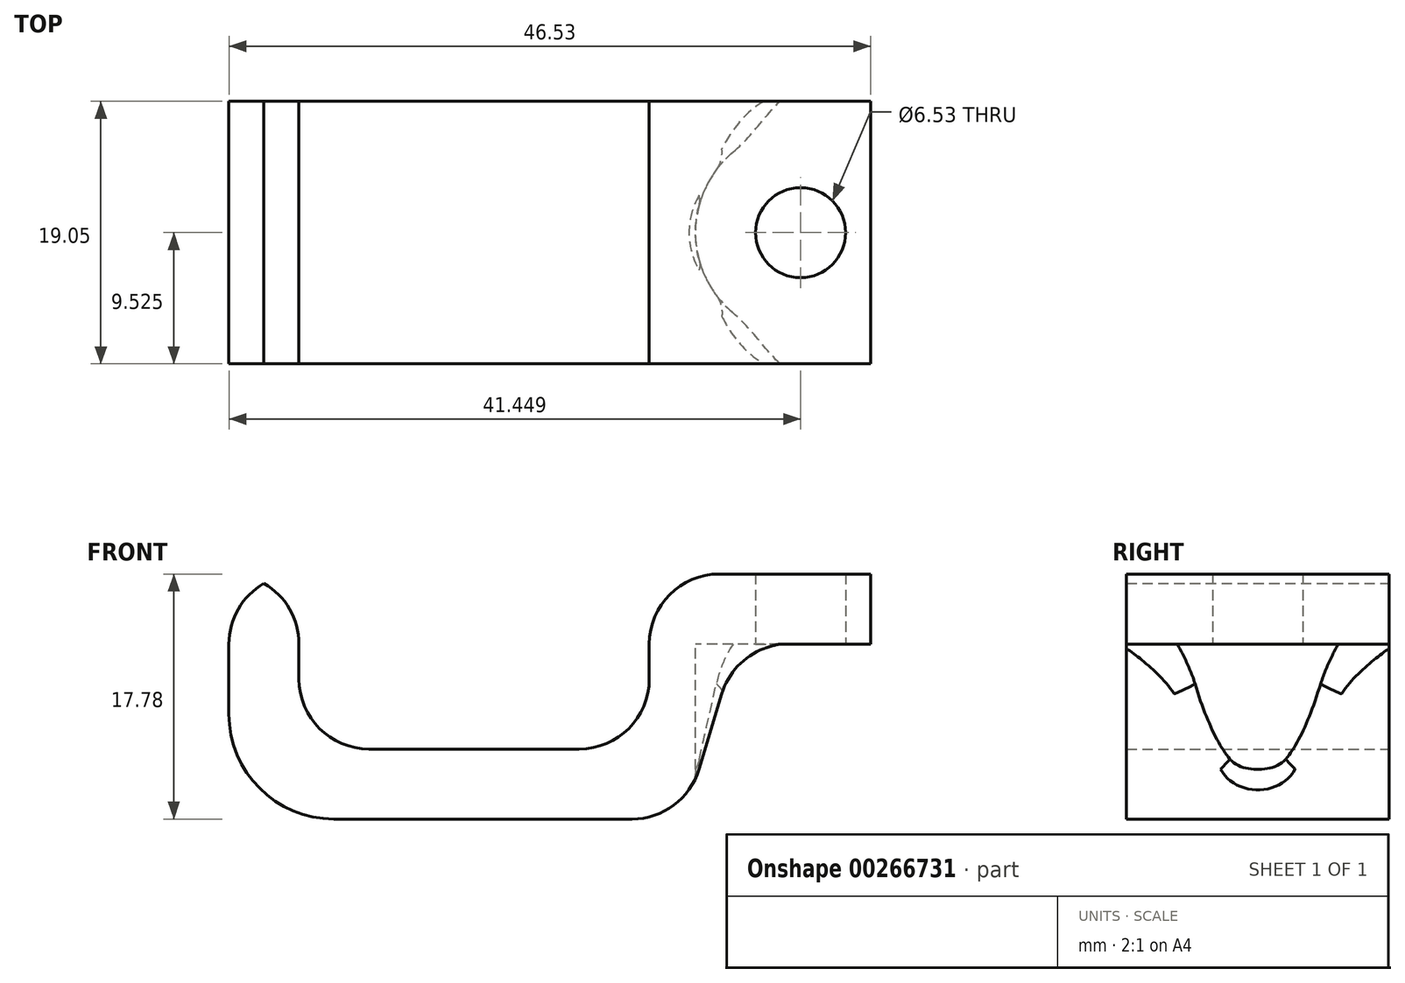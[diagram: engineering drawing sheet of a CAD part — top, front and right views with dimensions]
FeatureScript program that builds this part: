
annotation { "Feature Type Name" : "Feature", "Feature Type Description" : "" }
export const myFeature = defineFeature(function(context is Context, id is Id, definition is map)
    precondition{}
    {
        {
            var Q0;
            Q0=qCreatedBy(makeId("Front.planeOp"),FACE);
            var sketch = newSketch(context, id + "F0", { "sketchPlane" : qUnion([Q0])});
            skPoint(sketch, "E0.middle", {"position": v(0, 0) * mm});
            skLineSegment(sketch, "E1", {"start": v(26.17, 7.62) * mm, "end": v(16.47, 7.62) * mm});
            skLineSegment(sketch, "E2", {"start": v(-20.36, -5.08) * mm, "end": v(12.64, -5.08) * mm});
            skLineSegment(sketch, "E3", {"start": v(-15.28, 0) * mm, "end": v(10.12, 0) * mm});
            skLineSegment(sketch, "E4", {"start": v(-15.28, 0) * mm, "end": v(-15.28, 12.7) * mm});
            skLineSegment(sketch, "E5", {"start": v(-20.36, -5.08) * mm, "end": v(-20.36, 12.7) * mm});
            skLineSegment(sketch, "E6", {"start": v(10.12, 0) * mm, "end": v(10.12, 12.7) * mm});
            skLineSegment(sketch, "E7", {"start": v(16.47, 7.62) * mm, "end": v(12.64, -5.08) * mm});
            skLineSegment(sketch, "E8", {"start": v(-20.36, 12.7) * mm, "end": v(-15.28, 12.7) * mm});
            skLineSegment(sketch, "E9", {"start": v(10.12, 12.7) * mm, "end": v(26.17, 12.7) * mm});
            skLineSegment(sketch, "E10", {"start": v(26.17, 12.7) * mm, "end": v(26.17, 7.62) * mm});
            skSolve(sketch);
        }
        {
            var Q0;
            Q0 = qSketchRegion(id + "F0", true);
            extrude(context, id + "F1", {"entities" : qUnion([Q0]), "depth" : 19.05 * mm});
        }
        {
            var Q0;
            Q0=makeQuery(id+"F1.opExtrude","SWEPT_FACE",FACE,{"disambiguationData":[OSD([sQuery(id+"F0.wireOp",EDGE,"E1")])]});
            var sketch = newSketch(context, id + "F2", { "sketchPlane" : qUnion([Q0])});
            skCircle(sketch, "E11", {"center": v(21.09, 9.53) * mm, "radius": 3.27 * mm});
            skPoint(sketch, "E11.centerSnap0", {"position": v(26.17, 9.53) * mm});
            skCircle(sketch, "E12", {"center": v(21.09, 9.53) * mm, "radius": 7.62 * mm});
            skSolve(sketch);
        }
        {
            var Q0;
            Q0=makeQuery(id+"F2.imprint","IMPRINT",FACE,{"disambiguationData":[TD([[makeQuery(id+"F2.imprint","IMPRINT",EDGE,{"derivedFrom":sQuery(id+"F2.wireOp",EDGE,"E11")}),1.0]])]});
            extrude(context, id + "F3", {"entities" : qUnion([Q0]), "operationType" : NewBodyOperationType.REMOVE, "oppositeDirection" : true, "depth" : 25.4 * mm});
        }
        {
            var Q0;
            Q0=makeQuery(id+"F1.opExtrude","SWEPT_EDGE",EDGE,{"disambiguationData":[OSD([sQuery(id+"F0.wireOp",EDGE,"E3"),sQuery(id+"F0.wireOp",EDGE,"E4")])]});
            var Q1;
            Q1=makeQuery(id+"F1.opExtrude","SWEPT_EDGE",EDGE,{"disambiguationData":[OSD([sQuery(id+"F0.wireOp",EDGE,"E3"),sQuery(id+"F0.wireOp",EDGE,"E6")])]});
            var Q2;
            Q2=makeQuery(id+"F1.opExtrude","SWEPT_EDGE",EDGE,{"disambiguationData":[OSD([sQuery(id+"F0.wireOp",EDGE,"E2"),sQuery(id+"F0.wireOp",EDGE,"E7")])]});
            var Q3;
            Q3=makeQuery(id+"F1.opExtrude","SWEPT_EDGE",EDGE,{"disambiguationData":[OSD([sQuery(id+"F0.wireOp",EDGE,"E1"),sQuery(id+"F0.wireOp",EDGE,"E7")])]});
            var Q4;
            Q4=makeQuery(id+"F1.opExtrude","SWEPT_EDGE",EDGE,{"disambiguationData":[OSD([sQuery(id+"F0.wireOp",EDGE,"E6"),sQuery(id+"F0.wireOp",EDGE,"E9")])]});
            var Q5;
            Q5=makeQuery(id+"F1.opExtrude","SWEPT_EDGE",EDGE,{"disambiguationData":[OSD([sQuery(id+"F0.wireOp",EDGE,"E5"),sQuery(id+"F0.wireOp",EDGE,"E8")])]});
            var Q6;
            Q6=makeQuery(id+"F1.opExtrude","SWEPT_EDGE",EDGE,{"disambiguationData":[OSD([sQuery(id+"F0.wireOp",EDGE,"E4"),sQuery(id+"F0.wireOp",EDGE,"E8")])]});
            fillet(context, id + "F4", {"entities" : qUnion([Q0, Q1, Q2, Q3, Q4, Q5, Q6]), "radius" : 5.08 * mm, "tangentPropagation" : true, "allowEdgeOverflow" : false});
        }
        {
            var Q0;
            Q0 = qSketchRegion(id + "F2", true);
            extrude(context, id + "F5", {"entities" : qUnion([Q0]), "operationType" : NewBodyOperationType.REMOVE, "depth" : 25.4 * mm});
        }
        {
            var Q0;
            Q0=makeQuery(id+"F5.boolean.opBoolean","INTERSECT",EDGE,{"derivedFrom":[makeQuery(id+"F4.opFillet","BLEND_FACE",FACE,{"disambiguationData":[OSD([sQuery(id+"F0.wireOp",EDGE,"E1"),sQuery(id+"F0.wireOp",EDGE,"E7")]),OD(1.0)]}),makeQuery(id+"F5.opExtrude","SWEPT_FACE",FACE,{"disambiguationData":[OSD([sQuery(id+"F2.wireOp",EDGE,"E12")])]})]});
            var Q1;
            Q1=makeQuery(id+"F5.boolean.opBoolean","INTERSECT",EDGE,{"derivedFrom":[makeQuery(id+"F4.opFillet","BLEND_FACE",FACE,{"disambiguationData":[OSD([sQuery(id+"F0.wireOp",EDGE,"E1"),sQuery(id+"F0.wireOp",EDGE,"E7")]),OD(0.0)]}),makeQuery(id+"F5.opExtrude","SWEPT_FACE",FACE,{"disambiguationData":[OSD([sQuery(id+"F2.wireOp",EDGE,"E12")])]})]});
            fillet(context, id + "F6", {"entities" : qUnion([Q0, Q1]), "radius" : 2.54 * mm, "tangentPropagation" : true, "allowEdgeOverflow" : false});
        }
        {
            var Q0;
            Q0=makeQuery(id+"F1.opExtrude","SWEPT_EDGE",EDGE,{"disambiguationData":[OSD([sQuery(id+"F0.wireOp",EDGE,"E2"),sQuery(id+"F0.wireOp",EDGE,"E5")])]});
            fillet(context, id + "F7", {"entities" : qUnion([Q0]), "radius" : 7.62 * mm, "tangentPropagation" : true, "allowEdgeOverflow" : false});
        }
    });
